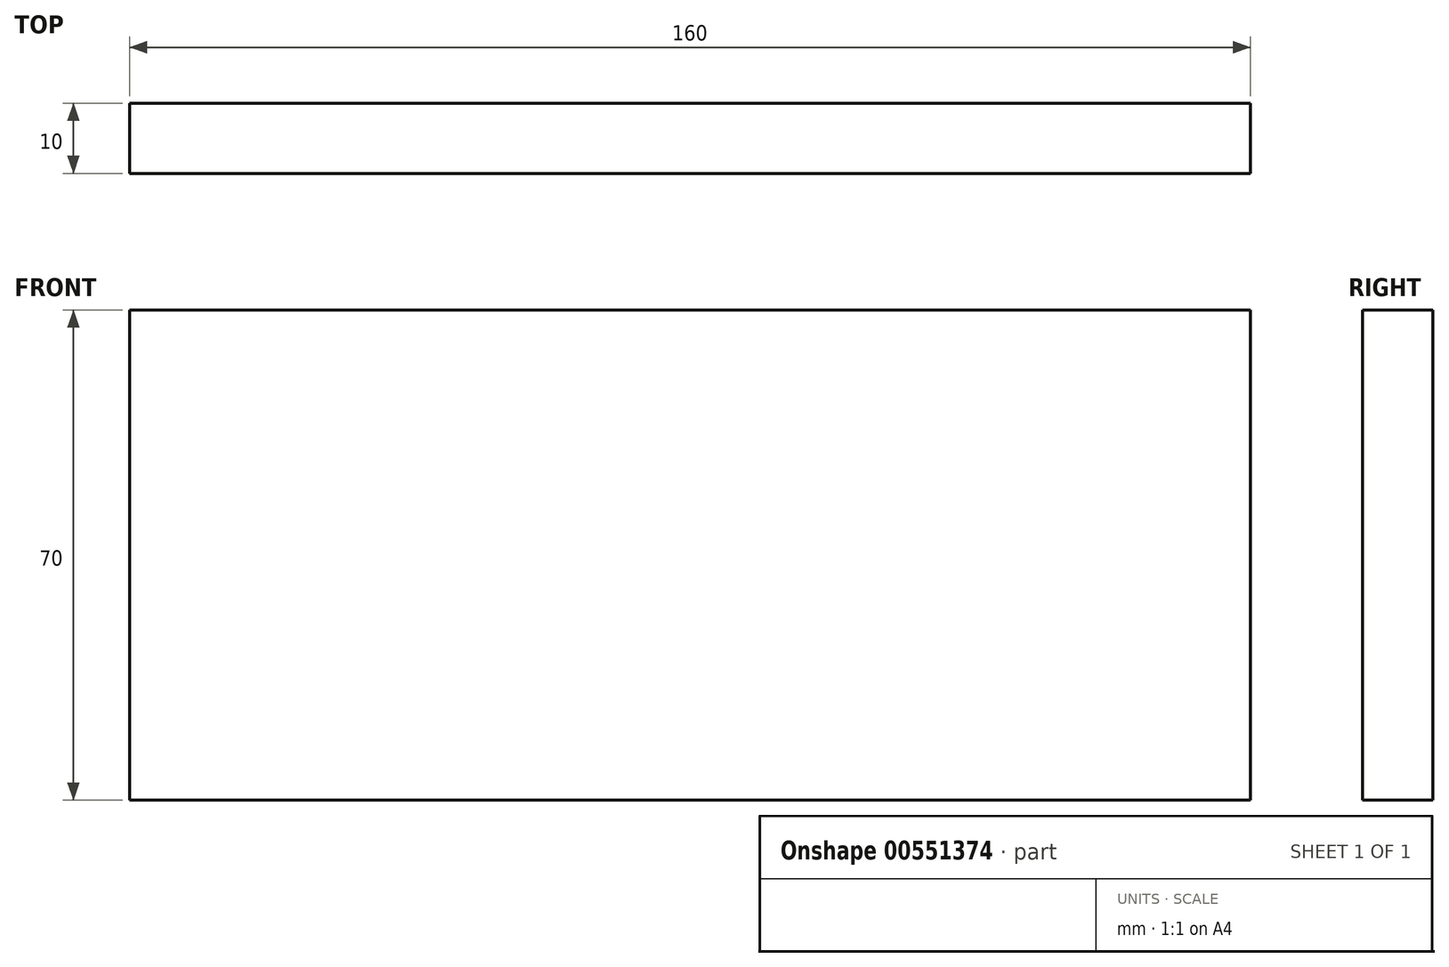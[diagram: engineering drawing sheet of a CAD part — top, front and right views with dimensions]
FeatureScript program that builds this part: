
annotation { "Feature Type Name" : "Feature", "Feature Type Description" : "" }
export const myFeature = defineFeature(function(context is Context, id is Id, definition is map)
    precondition{}
    {
        {
            var Q0;
            Q0=qCreatedBy(makeId("Front.planeOp"),FACE);
            var sketch = newSketch(context, id + "F0", { "sketchPlane" : qUnion([Q0])});
            skLineSegment(sketch, "E0.bottom", {"start": v(-83.44, 7.31) * mm, "end": v(76.56, 7.31) * mm});
            skLineSegment(sketch, "E0.top", {"start": v(-83.44, 77.31) * mm, "end": v(76.56, 77.31) * mm});
            skLineSegment(sketch, "E0.left", {"start": v(-83.44, 7.31) * mm, "end": v(-83.44, 77.31) * mm});
            skLineSegment(sketch, "E0.right", {"start": v(76.56, 7.31) * mm, "end": v(76.56, 77.31) * mm});
            skSolve(sketch);
        }
        {
            var Q0;
            Q0 = qSketchRegion(id + "F0", true);
            extrude(context, id + "F1", {"entities" : qUnion([Q0]), "depth" : 10 * mm, "offsetDistance" : 25 * mm});
        }
    });
